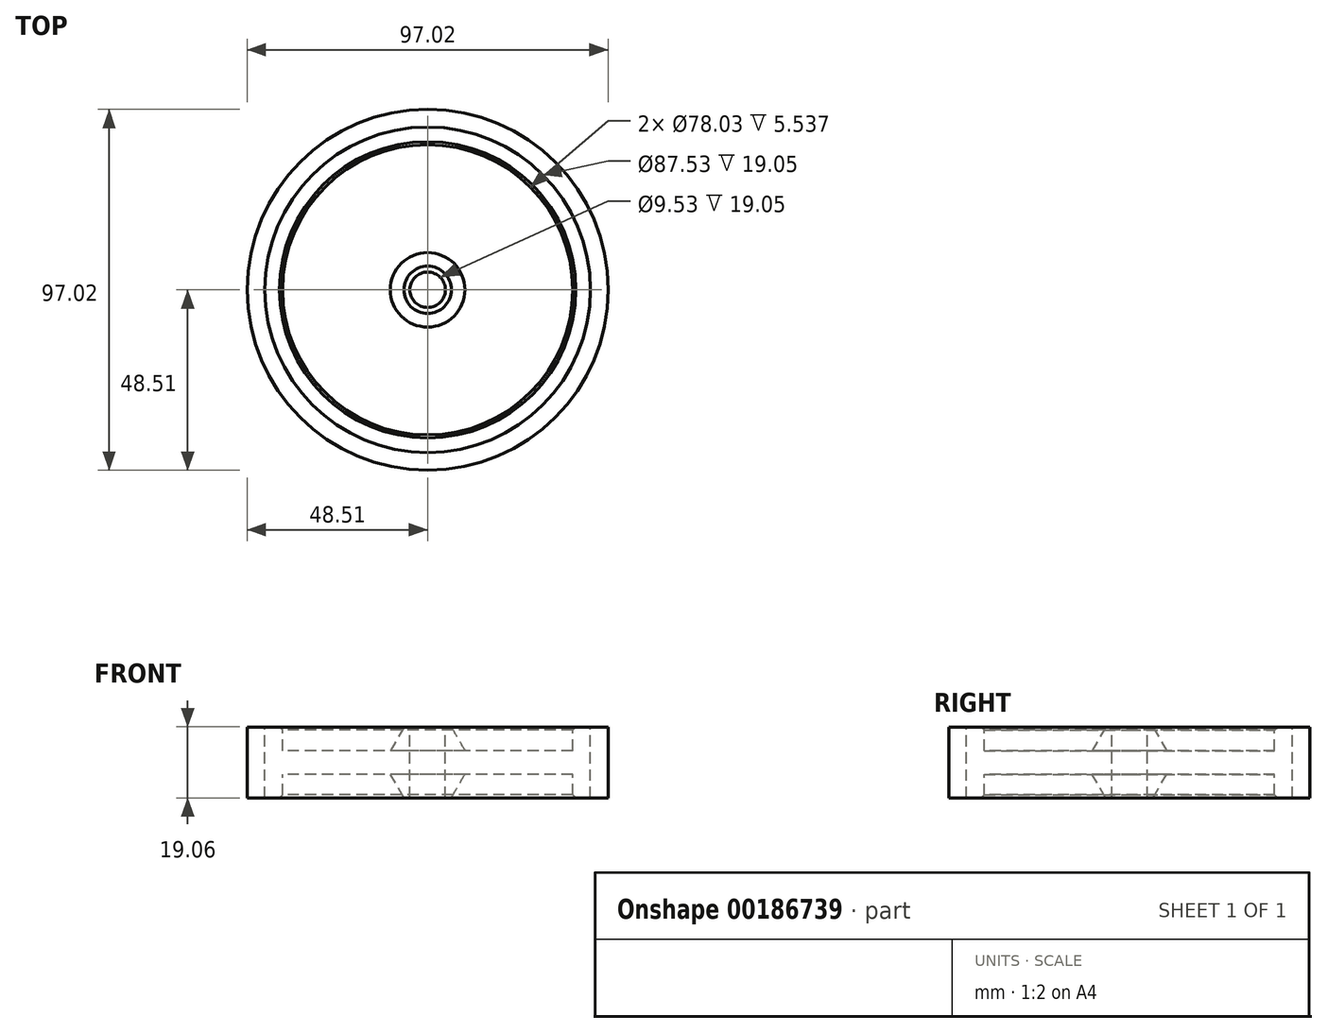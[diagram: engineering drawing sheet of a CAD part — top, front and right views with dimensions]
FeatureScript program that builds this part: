
annotation { "Feature Type Name" : "Feature", "Feature Type Description" : "" }
export const myFeature = defineFeature(function(context is Context, id is Id, definition is map)
    precondition{}
    {
        {
            var Q0;
            Q0=qCreatedBy(makeId("Front.planeOp"),FACE);
            var sketch = newSketch(context, id + "F0", { "sketchPlane" : qUnion([Q0])});
            skLineSegment(sketch, "E0", {"start": v(0, 9.53) * mm, "end": v(6.35, 9.53) * mm});
            skLineSegment(sketch, "E1", {"start": v(6.35, 9.53) * mm, "end": v(10.02, 3.17) * mm});
            skLineSegment(sketch, "E2", {"start": v(10.02, 3.18) * mm, "end": v(39.01, 3.18) * mm});
            skLineSegment(sketch, "E3", {"start": v(39.01, 3.18) * mm, "end": v(39.01, 9.53) * mm});
            skLineSegment(sketch, "E4", {"start": v(39.01, 9.53) * mm, "end": v(43.76, 9.53) * mm});
            skLineSegment(sketch, "E5", {"start": v(43.76, 9.53) * mm, "end": v(43.76, 0) * mm});
            skLineSegment(sketch, "E6", {"start": v(43.76, 9.53) * mm, "end": v(48.51, 9.53) * mm});
            skLineSegment(sketch, "E7", {"start": v(48.51, 9.53) * mm, "end": v(48.51, 0) * mm});
            skLineSegment(sketch, "E8.MirrorCS", {"start": v(48.51, -9.53) * mm, "end": v(48.51, 0) * mm});
            skLineSegment(sketch, "E9.MirrorCS", {"start": v(43.76, -9.53) * mm, "end": v(43.76, 0) * mm});
            skLineSegment(sketch, "E10.MirrorCS", {"start": v(43.76, -9.53) * mm, "end": v(48.51, -9.53) * mm});
            skLineSegment(sketch, "E11.MirrorCS", {"start": v(39.01, -3.18) * mm, "end": v(39.01, -9.53) * mm});
            skLineSegment(sketch, "E12.MirrorCS", {"start": v(39.01, -9.53) * mm, "end": v(43.76, -9.53) * mm});
            skLineSegment(sketch, "E13.MirrorCS", {"start": v(10.02, -3.18) * mm, "end": v(39.01, -3.18) * mm});
            skLineSegment(sketch, "E14.MirrorCS", {"start": v(6.35, -9.53) * mm, "end": v(10.02, -3.17) * mm});
            skLineSegment(sketch, "E15.MirrorCS", {"start": v(0, -9.53) * mm, "end": v(6.35, -9.53) * mm});
            skLineSegment(sketch, "E16", {"start": v(0, 9.53) * mm, "end": v(0, -9.53) * mm, "construction": true});
            skLineSegment(sketch, "E17", {"start": v(0, 9.53) * mm, "end": v(0, -9.53) * mm});
            skSolve(sketch);
        }
        {
            var Q0;
            Q0=makeQuery(id+"F0.imprint","IMPRINT",FACE,{"disambiguationData":[TD([[makeQuery(id+"F0.imprint","IMPRINT",EDGE,{"derivedFrom":sQuery(id+"F0.wireOp",EDGE,"E0")}),-1.0]])]});
            var Q1;
            Q1=sQuery(id+"F0.wireOp",EDGE,"E17");
            revolve(context, id + "F1", {"entities" : qUnion([Q0]), "axis" : qUnion([Q1]), "revolveType" : RevolveType.FULL});
        }
        {
            var Q0;
            Q0=makeQuery(id+"F0.imprint","IMPRINT",FACE,{"disambiguationData":[TD([[makeQuery(id+"F0.imprint","IMPRINT",EDGE,{"derivedFrom":sQuery(id+"F0.wireOp",EDGE,"E5")}),1.0]])]});
            var Q1;
            Q1=sQuery(id+"F0.wireOp",EDGE,"E17");
            revolve(context, id + "F2", {"entities" : qUnion([Q0]), "axis" : qUnion([Q1]), "revolveType" : RevolveType.FULL});
        }
        {
            var Q0;
            Q0=makeQuery(id+"F1.opRevolve","SWEPT_FACE",FACE,{"disambiguationData":[OSD([sQuery(id+"F0.wireOp",EDGE,"E0")])]});
            var sketch = newSketch(context, id + "F3", { "sketchPlane" : qUnion([Q0])});
            skCircle(sketch, "E18", {"center": v(0, 0) * mm, "radius": 4.76 * mm});
            skSolve(sketch);
        }
        {
            var Q0;
            Q0=makeQuery(id+"F3.imprint","IMPRINT",FACE,{"disambiguationData":[TD([[makeQuery(id+"F3.imprint","IMPRINT",EDGE,{"derivedFrom":sQuery(id+"F3.wireOp",EDGE,"E18")}),1.0]])]});
            extrude(context, id + "F4", {"entities" : qUnion([Q0]), "operationType" : NewBodyOperationType.REMOVE, "endBound" : BoundingType.THROUGH_ALL, "oppositeDirection" : true, "depth" : 25.4 * mm});
        }
        {
            var Q0;
            Q0=makeQuery(id+"F1.opRevolve","SWEPT_EDGE",EDGE,{"disambiguationData":[OSD([sQuery(id+"F0.wireOp",EDGE,"E3"),sQuery(id+"F0.wireOp",EDGE,"E4")])]});
            var Q1;
            Q1=makeQuery(id+"F1.opRevolve","SWEPT_EDGE",EDGE,{"disambiguationData":[OSD([sQuery(id+"F0.wireOp",EDGE,"E11.MirrorCS"),sQuery(id+"F0.wireOp",EDGE,"E12.MirrorCS")])]});
            chamfer(context, id + "F5", {"entities" : qUnion([Q0, Q1]), "width" : 0.81 * mm, "tangentPropagation" : true});
        }
    });
